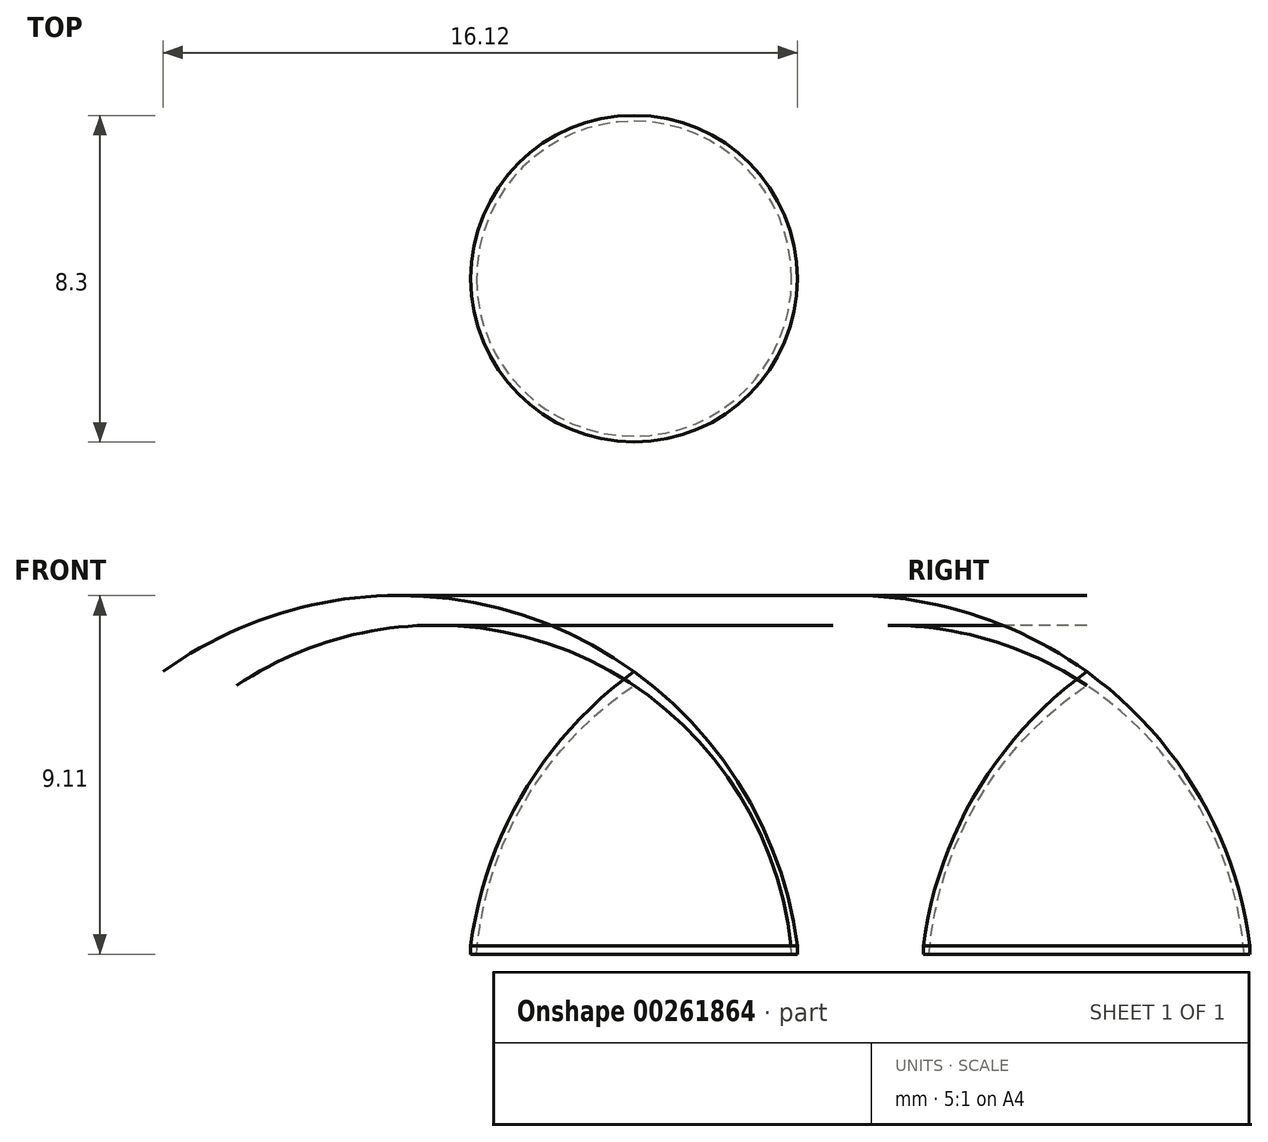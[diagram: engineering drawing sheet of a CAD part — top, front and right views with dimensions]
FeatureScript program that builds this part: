
annotation { "Feature Type Name" : "Feature", "Feature Type Description" : "" }
export const myFeature = defineFeature(function(context is Context, id is Id, definition is map)
    precondition{}
    {
        {
            var Q0;
            Q0=qCreatedBy(makeId("Top.planeOp"),FACE);
            var sketch = newSketch(context, id + "F0", { "sketchPlane" : qUnion([Q0])});
            skCircle(sketch, "E0", {"center": v(0, 0) * mm, "radius": 4.1 * mm});
            skSolve(sketch);
        }
        {
            var Q0;
            Q0=qCreatedBy(makeId("Right.planeOp"),FACE);
            var sketch = newSketch(context, id + "F1", { "sketchPlane" : qUnion([Q0])});
            skArc(sketch, "E1", {"start": v(0, 7.18) * mm, "mid": v(-2.8, 4.12) * mm, "end": v(-4.15, 0.2) * mm});
            skLineSegment(sketch, "E2", {"start": v(-4.15, 0) * mm, "end": v(-4.15, 0.2) * mm});
            skLineSegment(sketch, "E3", {"start": v(0, 7.18) * mm, "end": v(0, 6.82) * mm});
            skArc(sketch, "E4", {"start": v(0, 6.82) * mm, "mid": v(-2.78, 3.87) * mm, "end": v(-4, 0) * mm});
            skLineSegment(sketch, "E5", {"start": v(-4.15, 0) * mm, "end": v(-4, 0) * mm});
            skSolve(sketch);
        }
        {
            var Q0;
            Q0=makeQuery(id+"F1.imprint","IMPRINT",FACE,{"disambiguationData":[TD([[makeQuery(id+"F1.imprint","IMPRINT",EDGE,{"derivedFrom":sQuery(id+"F1.wireOp",EDGE,"E1")}),1.0]])]});
            var Q1;
            Q1=sQuery(id+"F0.wireOp",EDGE,"E0");
            revolve(context, id + "F2", {"entities" : qUnion([Q0]), "axis" : qUnion([Q1]), "revolveType" : RevolveType.FULL});
        }
    });
